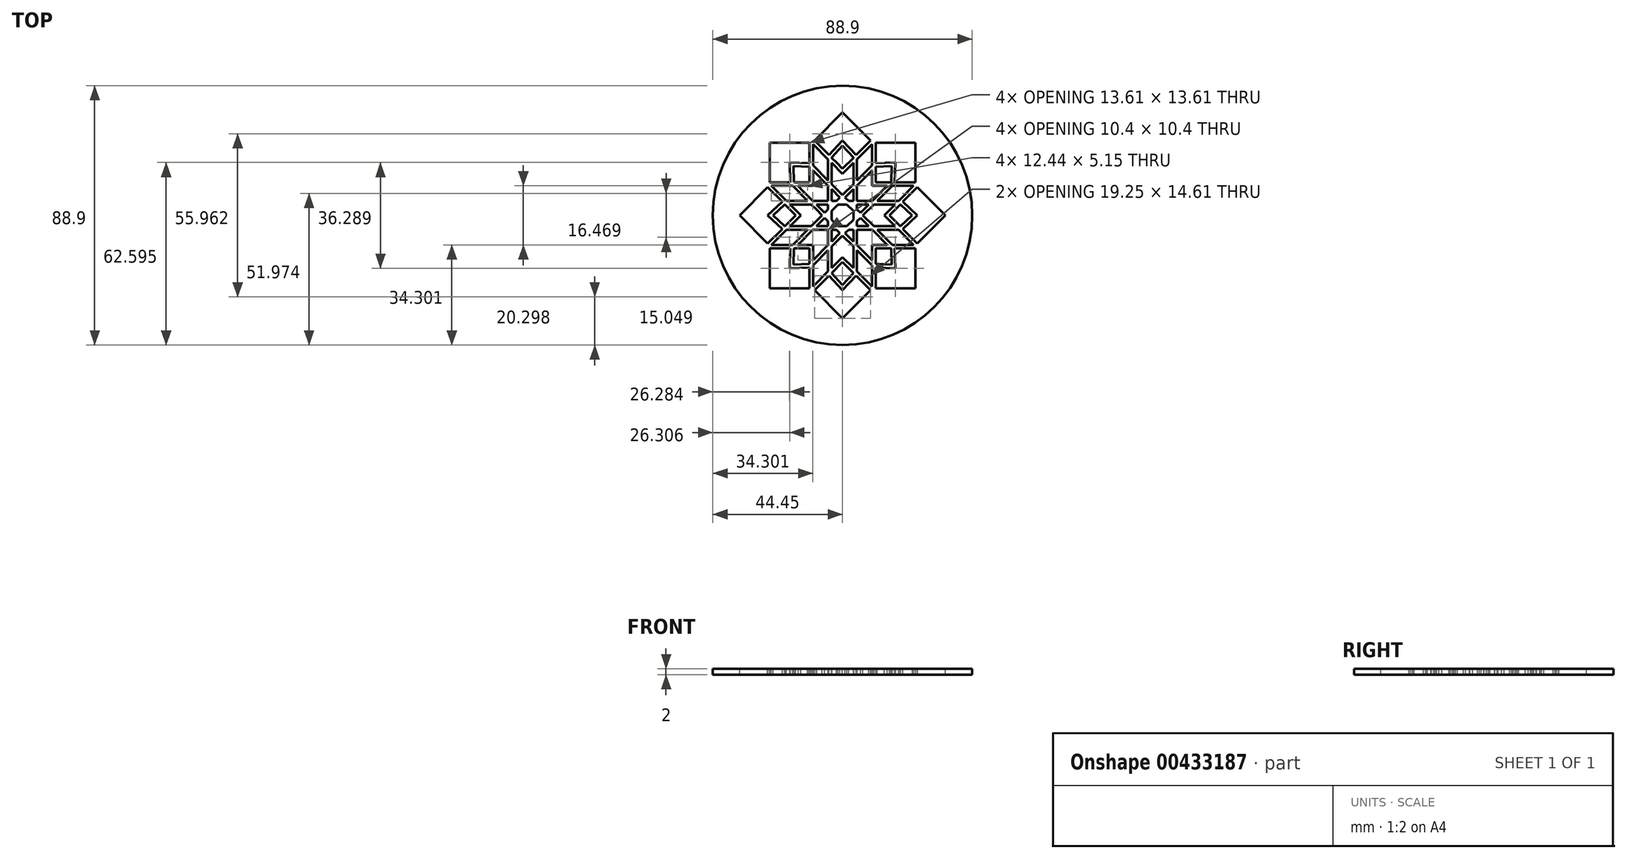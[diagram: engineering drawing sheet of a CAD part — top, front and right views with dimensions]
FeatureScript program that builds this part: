
annotation { "Feature Type Name" : "Feature", "Feature Type Description" : "" }
export const myFeature = defineFeature(function(context is Context, id is Id, definition is map)
    precondition{}
    {
        {
            var Q0;
            Q0=qCreatedBy(makeId("Top.planeOp"),FACE);
            var sketch = newSketch(context, id + "F0", { "sketchPlane" : qUnion([Q0])});
            skLineSegment(sketch, "E0.bottom", {"start": v(-44.45, 44.45) * mm, "end": v(44.45, 44.45) * mm});
            skLineSegment(sketch, "E0.top", {"start": v(-44.45, -44.45) * mm, "end": v(44.45, -44.45) * mm});
            skLineSegment(sketch, "E0.left", {"start": v(-44.45, 44.45) * mm, "end": v(-44.45, -44.45) * mm});
            skLineSegment(sketch, "E0.right", {"start": v(44.45, 44.45) * mm, "end": v(44.45, -44.45) * mm});
            skSolve(sketch);
        }
        {
            var Q0;
            Q0=qSketchRegion(id+"F0",true);
            extrude(context, id + "F1", {"entities" : qUnion([Q0]), "oppositeDirection" : true, "depth" : 2 * mm});
        }
        {
            var Q0;
            Q0=qCreatedBy(makeId("Top.planeOp"),FACE);
            var sketch = newSketch(context, id + "F2", { "sketchPlane" : qUnion([Q0])});
            skLineSegment(sketch, "E1", {"start": v(0.87, 6.12) * mm, "end": v(2.05, 4.95) * mm});
            skLineSegment(sketch, "E2", {"start": v(2.05, 4.95) * mm, "end": v(3.71, 4.95) * mm});
            skLineSegment(sketch, "E3", {"start": v(3.71, 4.95) * mm, "end": v(3.71, 8.96) * mm});
            skLineSegment(sketch, "E4", {"start": v(3.71, 8.96) * mm, "end": v(0.87, 6.12) * mm});
            skLineSegment(sketch, "E5", {"start": v(-3.71, 4.95) * mm, "end": v(-2.05, 4.95) * mm});
            skLineSegment(sketch, "E6", {"start": v(-2.05, 4.95) * mm, "end": v(-0.88, 6.12) * mm});
            skLineSegment(sketch, "E7", {"start": v(-0.88, 6.12) * mm, "end": v(-3.71, 8.96) * mm});
            skLineSegment(sketch, "E8", {"start": v(-3.71, 8.96) * mm, "end": v(-3.71, 4.95) * mm});
            skLineSegment(sketch, "E9", {"start": v(4.95, 3.71) * mm, "end": v(4.95, 2.05) * mm});
            skLineSegment(sketch, "E10", {"start": v(4.95, 2.05) * mm, "end": v(6.12, 0.88) * mm});
            skLineSegment(sketch, "E11", {"start": v(6.12, 0.88) * mm, "end": v(8.96, 3.71) * mm});
            skLineSegment(sketch, "E12", {"start": v(8.96, 3.71) * mm, "end": v(4.95, 3.71) * mm});
            skLineSegment(sketch, "E13", {"start": v(-0.88, -6.12) * mm, "end": v(-2.05, -4.95) * mm});
            skLineSegment(sketch, "E14", {"start": v(-2.05, -4.95) * mm, "end": v(-3.71, -4.95) * mm});
            skLineSegment(sketch, "E15", {"start": v(-3.71, -4.95) * mm, "end": v(-3.71, -8.96) * mm});
            skLineSegment(sketch, "E16", {"start": v(-3.71, -8.96) * mm, "end": v(-0.88, -6.12) * mm});
            skLineSegment(sketch, "E17", {"start": v(-4.95, -2.05) * mm, "end": v(-6.12, -0.87) * mm});
            skLineSegment(sketch, "E18", {"start": v(-6.12, -0.87) * mm, "end": v(-8.96, -3.71) * mm});
            skLineSegment(sketch, "E19", {"start": v(-8.96, -3.71) * mm, "end": v(-4.95, -3.71) * mm});
            skLineSegment(sketch, "E20", {"start": v(-4.95, -3.71) * mm, "end": v(-4.95, -2.05) * mm});
            skLineSegment(sketch, "E21", {"start": v(-14.28, 0) * mm, "end": v(-18, -3.71) * mm});
            skLineSegment(sketch, "E22", {"start": v(-18, -3.71) * mm, "end": v(-10.71, -3.71) * mm});
            skLineSegment(sketch, "E23", {"start": v(-10.71, -3.71) * mm, "end": v(-7, 0) * mm});
            skLineSegment(sketch, "E24", {"start": v(-7, 0) * mm, "end": v(-10.71, 3.71) * mm});
            skLineSegment(sketch, "E25", {"start": v(-10.71, 3.71) * mm, "end": v(-18, 3.71) * mm});
            skLineSegment(sketch, "E26", {"start": v(-18, 3.71) * mm, "end": v(-14.28, 0) * mm});
            skLineSegment(sketch, "E27", {"start": v(-8.96, 3.71) * mm, "end": v(-6.12, 0.88) * mm});
            skLineSegment(sketch, "E28", {"start": v(0, -7) * mm, "end": v(-3.71, -10.7) * mm});
            skLineSegment(sketch, "E29", {"start": v(-3.71, -10.7) * mm, "end": v(-3.71, -18) * mm});
            skLineSegment(sketch, "E30", {"start": v(-3.71, -18) * mm, "end": v(0, -14.28) * mm});
            skLineSegment(sketch, "E31", {"start": v(0, -14.28) * mm, "end": v(3.71, -18) * mm});
            skLineSegment(sketch, "E32", {"start": v(3.71, -18) * mm, "end": v(3.71, -10.7) * mm});
            skLineSegment(sketch, "E33", {"start": v(3.71, -10.7) * mm, "end": v(0, -7) * mm});
            skLineSegment(sketch, "E34", {"start": v(-10.1, -17.1) * mm, "end": v(-10.1, -24.38) * mm});
            skLineSegment(sketch, "E35", {"start": v(-10.1, -24.38) * mm, "end": v(-4.95, -19.23) * mm});
            skLineSegment(sketch, "E36", {"start": v(-4.95, -19.23) * mm, "end": v(-4.95, -11.95) * mm});
            skLineSegment(sketch, "E37", {"start": v(-4.95, -11.95) * mm, "end": v(-10.1, -17.1) * mm});
            skLineSegment(sketch, "E38", {"start": v(1.54, -3.71) * mm, "end": v(3.71, -1.54) * mm});
            skLineSegment(sketch, "E39", {"start": v(3.71, -1.54) * mm, "end": v(3.71, 1.54) * mm});
            skLineSegment(sketch, "E40", {"start": v(3.71, 1.54) * mm, "end": v(1.54, 3.71) * mm});
            skLineSegment(sketch, "E41", {"start": v(1.54, 3.71) * mm, "end": v(-1.54, 3.71) * mm});
            skLineSegment(sketch, "E42", {"start": v(-1.54, 3.71) * mm, "end": v(-3.71, 1.54) * mm});
            skLineSegment(sketch, "E43", {"start": v(-3.71, 1.54) * mm, "end": v(-3.71, -1.54) * mm});
            skLineSegment(sketch, "E44", {"start": v(-3.71, -1.54) * mm, "end": v(-1.54, -3.71) * mm});
            skLineSegment(sketch, "E45", {"start": v(-1.54, -3.71) * mm, "end": v(1.54, -3.71) * mm});
            skLineSegment(sketch, "E46", {"start": v(3.71, -19.86) * mm, "end": v(3.71, -19.75) * mm});
            skLineSegment(sketch, "E47", {"start": v(3.71, -19.75) * mm, "end": v(0, -16.03) * mm});
            skLineSegment(sketch, "E48", {"start": v(0, -16.03) * mm, "end": v(-3.71, -19.74) * mm});
            skLineSegment(sketch, "E49", {"start": v(-3.71, -19.74) * mm, "end": v(-3.71, -19.86) * mm});
            skLineSegment(sketch, "E50", {"start": v(-3.71, -19.86) * mm, "end": v(0, -23.84) * mm});
            skLineSegment(sketch, "E51", {"start": v(0, -23.84) * mm, "end": v(3.71, -19.86) * mm});
            skLineSegment(sketch, "E52", {"start": v(11.34, -16.59) * mm, "end": v(11.42, -16.67) * mm});
            skLineSegment(sketch, "E53", {"start": v(11.42, -16.67) * mm, "end": v(16.86, -16.86) * mm});
            skLineSegment(sketch, "E54", {"start": v(16.86, -16.86) * mm, "end": v(16.67, -11.42) * mm});
            skLineSegment(sketch, "E55", {"start": v(16.67, -11.42) * mm, "end": v(16.59, -11.34) * mm});
            skLineSegment(sketch, "E56", {"start": v(16.59, -11.34) * mm, "end": v(11.34, -11.34) * mm});
            skLineSegment(sketch, "E57", {"start": v(11.34, -11.34) * mm, "end": v(11.34, -16.59) * mm});
            skLineSegment(sketch, "E58", {"start": v(-19.75, 3.71) * mm, "end": v(-19.86, 3.71) * mm});
            skLineSegment(sketch, "E59", {"start": v(-19.86, 3.71) * mm, "end": v(-23.84, 0) * mm});
            skLineSegment(sketch, "E60", {"start": v(-23.84, 0) * mm, "end": v(-19.86, -3.71) * mm});
            skLineSegment(sketch, "E61", {"start": v(-19.86, -3.71) * mm, "end": v(-19.75, -3.71) * mm});
            skLineSegment(sketch, "E62", {"start": v(-19.75, -3.71) * mm, "end": v(-16.03, 0) * mm});
            skLineSegment(sketch, "E63", {"start": v(-16.03, 0) * mm, "end": v(-19.75, 3.71) * mm});
            skLineSegment(sketch, "E64", {"start": v(10.1, 17.1) * mm, "end": v(10.1, 24.39) * mm});
            skLineSegment(sketch, "E65", {"start": v(10.1, 24.39) * mm, "end": v(4.95, 19.23) * mm});
            skLineSegment(sketch, "E66", {"start": v(4.95, 19.23) * mm, "end": v(4.95, 11.95) * mm});
            skLineSegment(sketch, "E67", {"start": v(4.95, 11.95) * mm, "end": v(10.1, 17.1) * mm});
            skLineSegment(sketch, "E68", {"start": v(19.75, -3.71) * mm, "end": v(19.86, -3.71) * mm});
            skLineSegment(sketch, "E69", {"start": v(19.86, -3.71) * mm, "end": v(23.84, 0) * mm});
            skLineSegment(sketch, "E70", {"start": v(23.84, 0) * mm, "end": v(19.86, 3.71) * mm});
            skLineSegment(sketch, "E71", {"start": v(19.86, 3.71) * mm, "end": v(19.75, 3.71) * mm});
            skLineSegment(sketch, "E72", {"start": v(19.75, 3.71) * mm, "end": v(16.03, 0) * mm});
            skLineSegment(sketch, "E73", {"start": v(16.03, 0) * mm, "end": v(19.75, -3.71) * mm});
            skLineSegment(sketch, "E74", {"start": v(0, 7) * mm, "end": v(3.71, 10.71) * mm});
            skLineSegment(sketch, "E75", {"start": v(3.71, 10.71) * mm, "end": v(3.71, 18) * mm});
            skLineSegment(sketch, "E76", {"start": v(3.71, 18) * mm, "end": v(0, 14.29) * mm});
            skLineSegment(sketch, "E77", {"start": v(0, 14.29) * mm, "end": v(-3.71, 18) * mm});
            skLineSegment(sketch, "E78", {"start": v(-3.71, 18) * mm, "end": v(-3.71, 10.71) * mm});
            skLineSegment(sketch, "E79", {"start": v(-3.71, 10.71) * mm, "end": v(0, 7) * mm});
            skLineSegment(sketch, "E80", {"start": v(-3.71, 19.86) * mm, "end": v(-3.71, 19.75) * mm});
            skLineSegment(sketch, "E81", {"start": v(-3.71, 19.75) * mm, "end": v(0, 16.03) * mm});
            skLineSegment(sketch, "E82", {"start": v(0, 16.03) * mm, "end": v(3.71, 19.75) * mm});
            skLineSegment(sketch, "E83", {"start": v(3.71, 19.75) * mm, "end": v(3.71, 19.86) * mm});
            skLineSegment(sketch, "E84", {"start": v(3.71, 19.86) * mm, "end": v(0, 23.84) * mm});
            skLineSegment(sketch, "E85", {"start": v(0, 23.84) * mm, "end": v(-3.71, 19.86) * mm});
            skLineSegment(sketch, "E86", {"start": v(10.1, -17.1) * mm, "end": v(4.95, -11.95) * mm});
            skLineSegment(sketch, "E87", {"start": v(4.95, -11.95) * mm, "end": v(4.95, -19.23) * mm});
            skLineSegment(sketch, "E88", {"start": v(4.95, -19.23) * mm, "end": v(10.1, -24.38) * mm});
            skLineSegment(sketch, "E89", {"start": v(10.1, -24.38) * mm, "end": v(10.1, -17.1) * mm});
            skLineSegment(sketch, "E90", {"start": v(11.34, 17.9) * mm, "end": v(18.14, 18.14) * mm});
            skLineSegment(sketch, "E91", {"start": v(18.14, 18.14) * mm, "end": v(17.9, 11.34) * mm});
            skLineSegment(sketch, "E92", {"start": v(17.9, 11.34) * mm, "end": v(24.95, 11.34) * mm});
            skLineSegment(sketch, "E93", {"start": v(24.95, 11.34) * mm, "end": v(24.95, 24.95) * mm});
            skLineSegment(sketch, "E94", {"start": v(24.95, 24.95) * mm, "end": v(11.34, 24.95) * mm});
            skLineSegment(sketch, "E95", {"start": v(11.34, 24.95) * mm, "end": v(11.34, 17.9) * mm});
            skLineSegment(sketch, "E96", {"start": v(0, 25.65) * mm, "end": v(4.64, 20.68) * mm});
            skLineSegment(sketch, "E97", {"start": v(4.64, 20.68) * mm, "end": v(9.63, 25.66) * mm});
            skLineSegment(sketch, "E98", {"start": v(9.63, 25.66) * mm, "end": v(0, 35.29) * mm});
            skLineSegment(sketch, "E99", {"start": v(0, 35.29) * mm, "end": v(-9.63, 25.66) * mm});
            skLineSegment(sketch, "E100", {"start": v(-9.63, 25.66) * mm, "end": v(-4.64, 20.68) * mm});
            skLineSegment(sketch, "E101", {"start": v(-4.64, 20.68) * mm, "end": v(0, 25.65) * mm});
            skLineSegment(sketch, "E102", {"start": v(20.68, 4.64) * mm, "end": v(25.65, 0) * mm});
            skLineSegment(sketch, "E103", {"start": v(25.65, 0) * mm, "end": v(20.68, -4.64) * mm});
            skLineSegment(sketch, "E104", {"start": v(20.68, -4.64) * mm, "end": v(25.66, -9.63) * mm});
            skLineSegment(sketch, "E105", {"start": v(25.66, -9.63) * mm, "end": v(35.29, 0) * mm});
            skLineSegment(sketch, "E106", {"start": v(35.29, 0) * mm, "end": v(25.66, 9.63) * mm});
            skLineSegment(sketch, "E107", {"start": v(25.66, 9.63) * mm, "end": v(20.68, 4.64) * mm});
            skLineSegment(sketch, "E108", {"start": v(-18.14, 18.14) * mm, "end": v(-11.34, 17.9) * mm});
            skLineSegment(sketch, "E109", {"start": v(-11.34, 17.9) * mm, "end": v(-11.34, 24.95) * mm});
            skLineSegment(sketch, "E110", {"start": v(-11.34, 24.95) * mm, "end": v(-24.95, 24.95) * mm});
            skLineSegment(sketch, "E111", {"start": v(-24.95, 24.95) * mm, "end": v(-24.95, 11.34) * mm});
            skLineSegment(sketch, "E112", {"start": v(-24.95, 11.34) * mm, "end": v(-17.9, 11.34) * mm});
            skLineSegment(sketch, "E113", {"start": v(-17.9, 11.34) * mm, "end": v(-18.14, 18.14) * mm});
            skLineSegment(sketch, "E114", {"start": v(15.35, -10.1) * mm, "end": v(10.2, -4.95) * mm});
            skLineSegment(sketch, "E115", {"start": v(10.2, -4.95) * mm, "end": v(4.95, -4.95) * mm});
            skLineSegment(sketch, "E116", {"start": v(4.95, -4.95) * mm, "end": v(4.95, -10.2) * mm});
            skLineSegment(sketch, "E117", {"start": v(4.95, -10.2) * mm, "end": v(10.1, -15.35) * mm});
            skLineSegment(sketch, "E118", {"start": v(10.1, -15.35) * mm, "end": v(10.1, -10.1) * mm});
            skLineSegment(sketch, "E119", {"start": v(10.1, -10.1) * mm, "end": v(15.35, -10.1) * mm});
            skLineSegment(sketch, "E120", {"start": v(19.23, -4.95) * mm, "end": v(11.95, -4.95) * mm});
            skLineSegment(sketch, "E121", {"start": v(11.95, -4.95) * mm, "end": v(17.1, -10.1) * mm});
            skLineSegment(sketch, "E122", {"start": v(17.1, -10.1) * mm, "end": v(24.38, -10.1) * mm});
            skLineSegment(sketch, "E123", {"start": v(24.38, -10.1) * mm, "end": v(19.23, -4.95) * mm});
            skLineSegment(sketch, "E124", {"start": v(-20.68, -4.64) * mm, "end": v(-25.65, 0) * mm});
            skLineSegment(sketch, "E125", {"start": v(-25.65, 0) * mm, "end": v(-20.68, 4.64) * mm});
            skLineSegment(sketch, "E126", {"start": v(-20.68, 4.64) * mm, "end": v(-25.66, 9.63) * mm});
            skLineSegment(sketch, "E127", {"start": v(-25.66, 9.63) * mm, "end": v(-35.29, 0) * mm});
            skLineSegment(sketch, "E128", {"start": v(-35.29, 0) * mm, "end": v(-25.66, -9.63) * mm});
            skLineSegment(sketch, "E129", {"start": v(-25.66, -9.63) * mm, "end": v(-20.68, -4.64) * mm});
            skLineSegment(sketch, "E130", {"start": v(-4.95, -10.2) * mm, "end": v(-4.95, -4.95) * mm});
            skLineSegment(sketch, "E131", {"start": v(-4.95, -4.95) * mm, "end": v(-10.2, -4.95) * mm});
            skLineSegment(sketch, "E132", {"start": v(-10.2, -4.95) * mm, "end": v(-15.35, -10.1) * mm});
            skLineSegment(sketch, "E133", {"start": v(-15.35, -10.1) * mm, "end": v(-10.1, -10.1) * mm});
            skLineSegment(sketch, "E134", {"start": v(-10.1, -10.1) * mm, "end": v(-10.1, -15.35) * mm});
            skLineSegment(sketch, "E135", {"start": v(-10.1, -15.35) * mm, "end": v(-4.95, -10.2) * mm});
            skLineSegment(sketch, "E136", {"start": v(3.71, -4.95) * mm, "end": v(2.05, -4.95) * mm});
            skLineSegment(sketch, "E137", {"start": v(2.05, -4.95) * mm, "end": v(0.87, -6.12) * mm});
            skLineSegment(sketch, "E138", {"start": v(0.87, -6.12) * mm, "end": v(3.71, -8.96) * mm});
            skLineSegment(sketch, "E139", {"start": v(3.71, -8.96) * mm, "end": v(3.71, -4.95) * mm});
            skLineSegment(sketch, "E140", {"start": v(0, -35.29) * mm, "end": v(9.63, -25.66) * mm});
            skLineSegment(sketch, "E141", {"start": v(9.63, -25.66) * mm, "end": v(4.64, -20.68) * mm});
            skLineSegment(sketch, "E142", {"start": v(4.64, -20.68) * mm, "end": v(0, -25.65) * mm});
            skLineSegment(sketch, "E143", {"start": v(0, -25.65) * mm, "end": v(-4.64, -20.68) * mm});
            skLineSegment(sketch, "E144", {"start": v(-4.64, -20.68) * mm, "end": v(-9.63, -25.66) * mm});
            skLineSegment(sketch, "E145", {"start": v(-9.63, -25.66) * mm, "end": v(0, -35.29) * mm});
            skLineSegment(sketch, "E146", {"start": v(18.14, -18.14) * mm, "end": v(11.34, -17.9) * mm});
            skLineSegment(sketch, "E147", {"start": v(11.34, -17.9) * mm, "end": v(11.34, -24.95) * mm});
            skLineSegment(sketch, "E148", {"start": v(11.34, -24.95) * mm, "end": v(24.95, -24.95) * mm});
            skLineSegment(sketch, "E149", {"start": v(24.95, -24.95) * mm, "end": v(24.95, -11.34) * mm});
            skLineSegment(sketch, "E150", {"start": v(24.95, -11.34) * mm, "end": v(17.9, -11.34) * mm});
            skLineSegment(sketch, "E151", {"start": v(17.9, -11.34) * mm, "end": v(18.14, -18.14) * mm});
            skLineSegment(sketch, "E152", {"start": v(14.28, 0) * mm, "end": v(18, 3.71) * mm});
            skLineSegment(sketch, "E153", {"start": v(18, 3.71) * mm, "end": v(10.7, 3.71) * mm});
            skLineSegment(sketch, "E154", {"start": v(10.7, 3.71) * mm, "end": v(7, 0) * mm});
            skLineSegment(sketch, "E155", {"start": v(7, 0) * mm, "end": v(10.7, -3.71) * mm});
            skLineSegment(sketch, "E156", {"start": v(10.7, -3.71) * mm, "end": v(18, -3.71) * mm});
            skLineSegment(sketch, "E157", {"start": v(18, -3.71) * mm, "end": v(14.28, 0) * mm});
            skLineSegment(sketch, "E158", {"start": v(4.95, 10.2) * mm, "end": v(4.95, 4.95) * mm});
            skLineSegment(sketch, "E159", {"start": v(4.95, 4.95) * mm, "end": v(10.2, 4.95) * mm});
            skLineSegment(sketch, "E160", {"start": v(10.2, 4.95) * mm, "end": v(15.35, 10.1) * mm});
            skLineSegment(sketch, "E161", {"start": v(15.35, 10.1) * mm, "end": v(10.1, 10.1) * mm});
            skLineSegment(sketch, "E162", {"start": v(10.1, 10.1) * mm, "end": v(10.1, 15.35) * mm});
            skLineSegment(sketch, "E163", {"start": v(10.1, 15.35) * mm, "end": v(4.95, 10.2) * mm});
            skLineSegment(sketch, "E164", {"start": v(11.34, 16.59) * mm, "end": v(11.34, 11.34) * mm});
            skLineSegment(sketch, "E165", {"start": v(11.34, 11.34) * mm, "end": v(16.59, 11.34) * mm});
            skLineSegment(sketch, "E166", {"start": v(16.59, 11.34) * mm, "end": v(16.67, 11.42) * mm});
            skLineSegment(sketch, "E167", {"start": v(16.67, 11.42) * mm, "end": v(16.86, 16.86) * mm});
            skLineSegment(sketch, "E168", {"start": v(16.86, 16.86) * mm, "end": v(11.42, 16.67) * mm});
            skLineSegment(sketch, "E169", {"start": v(11.42, 16.67) * mm, "end": v(11.34, 16.59) * mm});
            skLineSegment(sketch, "E170", {"start": v(17.1, 10.1) * mm, "end": v(11.95, 4.95) * mm});
            skLineSegment(sketch, "E171", {"start": v(11.95, 4.95) * mm, "end": v(19.23, 4.95) * mm});
            skLineSegment(sketch, "E172", {"start": v(19.23, 4.95) * mm, "end": v(24.38, 10.1) * mm});
            skLineSegment(sketch, "E173", {"start": v(24.38, 10.1) * mm, "end": v(17.1, 10.1) * mm});
            skLineSegment(sketch, "E174", {"start": v(6.12, -0.87) * mm, "end": v(4.95, -2.05) * mm});
            skLineSegment(sketch, "E175", {"start": v(4.95, -2.05) * mm, "end": v(4.95, -3.71) * mm});
            skLineSegment(sketch, "E176", {"start": v(4.95, -3.71) * mm, "end": v(8.96, -3.71) * mm});
            skLineSegment(sketch, "E177", {"start": v(8.96, -3.71) * mm, "end": v(6.12, -0.87) * mm});
            skLineSegment(sketch, "E178", {"start": v(-24.38, -10.1) * mm, "end": v(-17.1, -10.1) * mm});
            skLineSegment(sketch, "E179", {"start": v(-10.1, 17.1) * mm, "end": v(-4.95, 11.95) * mm});
            skLineSegment(sketch, "E180", {"start": v(-4.95, 11.95) * mm, "end": v(-4.95, 19.23) * mm});
            skLineSegment(sketch, "E181", {"start": v(-4.95, 19.23) * mm, "end": v(-10.1, 24.39) * mm});
            skLineSegment(sketch, "E182", {"start": v(-10.1, 24.39) * mm, "end": v(-10.1, 17.1) * mm});
            skLineSegment(sketch, "E183", {"start": v(-19.23, 4.95) * mm, "end": v(-11.95, 4.95) * mm});
            skLineSegment(sketch, "E184", {"start": v(-11.95, 4.95) * mm, "end": v(-17.1, 10.1) * mm});
            skLineSegment(sketch, "E185", {"start": v(-17.1, 10.1) * mm, "end": v(-24.39, 10.1) * mm});
            skLineSegment(sketch, "E186", {"start": v(-24.39, 10.1) * mm, "end": v(-19.23, 4.95) * mm});
            skLineSegment(sketch, "E187", {"start": v(-15.35, 10.1) * mm, "end": v(-10.2, 4.95) * mm});
            skLineSegment(sketch, "E188", {"start": v(-10.2, 4.95) * mm, "end": v(-4.95, 4.95) * mm});
            skLineSegment(sketch, "E189", {"start": v(-4.95, 4.95) * mm, "end": v(-4.95, 10.2) * mm});
            skLineSegment(sketch, "E190", {"start": v(-4.95, 10.2) * mm, "end": v(-10.1, 15.35) * mm});
            skLineSegment(sketch, "E191", {"start": v(-10.1, 15.35) * mm, "end": v(-10.1, 10.1) * mm});
            skLineSegment(sketch, "E192", {"start": v(-10.1, 10.1) * mm, "end": v(-15.35, 10.1) * mm});
            skLineSegment(sketch, "E193", {"start": v(-11.34, -16.59) * mm, "end": v(-11.34, -11.34) * mm});
            skLineSegment(sketch, "E194", {"start": v(-11.34, -11.34) * mm, "end": v(-16.59, -11.34) * mm});
            skLineSegment(sketch, "E195", {"start": v(-16.59, -11.34) * mm, "end": v(-16.67, -11.42) * mm});
            skLineSegment(sketch, "E196", {"start": v(-16.67, -11.42) * mm, "end": v(-16.86, -16.86) * mm});
            skLineSegment(sketch, "E197", {"start": v(-16.86, -16.86) * mm, "end": v(-11.42, -16.67) * mm});
            skLineSegment(sketch, "E198", {"start": v(-11.42, -16.67) * mm, "end": v(-11.34, -16.59) * mm});
            skLineSegment(sketch, "E199", {"start": v(16.67, -11.42) * mm, "end": v(16.86, -16.86) * mm});
            skLineSegment(sketch, "E200", {"start": v(16.86, -16.86) * mm, "end": v(11.42, -16.67) * mm});
            skLineSegment(sketch, "E201", {"start": v(11.42, -16.67) * mm, "end": v(11.34, -16.59) * mm});
            skLineSegment(sketch, "E202", {"start": v(11.34, -16.59) * mm, "end": v(11.34, -11.34) * mm});
            skLineSegment(sketch, "E203", {"start": v(11.34, -11.34) * mm, "end": v(16.59, -11.34) * mm});
            skLineSegment(sketch, "E204", {"start": v(16.59, -11.34) * mm, "end": v(16.67, -11.42) * mm});
            skLineSegment(sketch, "E205", {"start": v(-3.71, -19.74) * mm, "end": v(0, -16.03) * mm});
            skLineSegment(sketch, "E206", {"start": v(0, -16.03) * mm, "end": v(3.71, -19.75) * mm});
            skLineSegment(sketch, "E207", {"start": v(3.71, -19.75) * mm, "end": v(3.71, -19.86) * mm});
            skLineSegment(sketch, "E208", {"start": v(3.71, -19.86) * mm, "end": v(0, -23.84) * mm});
            skLineSegment(sketch, "E209", {"start": v(0, -23.84) * mm, "end": v(-3.71, -19.86) * mm});
            skLineSegment(sketch, "E210", {"start": v(-3.71, -19.86) * mm, "end": v(-3.71, -19.74) * mm});
            skLineSegment(sketch, "E211", {"start": v(0, -14.28) * mm, "end": v(-3.71, -18) * mm});
            skLineSegment(sketch, "E212", {"start": v(-3.71, -18) * mm, "end": v(-3.71, -10.7) * mm});
            skLineSegment(sketch, "E213", {"start": v(-3.71, -10.7) * mm, "end": v(0, -7) * mm});
            skLineSegment(sketch, "E214", {"start": v(0, -7) * mm, "end": v(3.71, -10.7) * mm});
            skLineSegment(sketch, "E215", {"start": v(3.71, -10.7) * mm, "end": v(3.71, -18) * mm});
            skLineSegment(sketch, "E216", {"start": v(3.71, -18) * mm, "end": v(0, -14.28) * mm});
            skLineSegment(sketch, "E217", {"start": v(-10.1, -24.38) * mm, "end": v(-10.1, -17.1) * mm});
            skLineSegment(sketch, "E218", {"start": v(-10.1, -17.1) * mm, "end": v(-4.95, -11.95) * mm});
            skLineSegment(sketch, "E219", {"start": v(-4.95, -11.95) * mm, "end": v(-4.95, -19.23) * mm});
            skLineSegment(sketch, "E220", {"start": v(-4.95, -19.23) * mm, "end": v(-10.1, -24.38) * mm});
            skLineSegment(sketch, "E221", {"start": v(-19.86, -3.71) * mm, "end": v(-23.84, 0) * mm});
            skLineSegment(sketch, "E222", {"start": v(-23.84, 0) * mm, "end": v(-19.86, 3.71) * mm});
            skLineSegment(sketch, "E223", {"start": v(-19.86, 3.71) * mm, "end": v(-19.75, 3.71) * mm});
            skLineSegment(sketch, "E224", {"start": v(-19.75, 3.71) * mm, "end": v(-16.03, 0) * mm});
            skLineSegment(sketch, "E225", {"start": v(-16.03, 0) * mm, "end": v(-19.75, -3.71) * mm});
            skLineSegment(sketch, "E226", {"start": v(-19.75, -3.71) * mm, "end": v(-19.86, -3.71) * mm});
            skLineSegment(sketch, "E227", {"start": v(3.71, 19.75) * mm, "end": v(0, 16.03) * mm});
            skLineSegment(sketch, "E228", {"start": v(0, 16.03) * mm, "end": v(-3.71, 19.75) * mm});
            skLineSegment(sketch, "E229", {"start": v(-3.71, 19.75) * mm, "end": v(-3.71, 19.86) * mm});
            skLineSegment(sketch, "E230", {"start": v(-3.71, 19.86) * mm, "end": v(0, 23.84) * mm});
            skLineSegment(sketch, "E231", {"start": v(0, 23.84) * mm, "end": v(3.71, 19.86) * mm});
            skLineSegment(sketch, "E232", {"start": v(3.71, 19.86) * mm, "end": v(3.71, 19.75) * mm});
            skLineSegment(sketch, "E233", {"start": v(0, 14.28) * mm, "end": v(3.71, 18) * mm});
            skLineSegment(sketch, "E234", {"start": v(3.71, 18) * mm, "end": v(3.71, 10.71) * mm});
            skLineSegment(sketch, "E235", {"start": v(3.71, 10.71) * mm, "end": v(0, 7) * mm});
            skLineSegment(sketch, "E236", {"start": v(0, 7) * mm, "end": v(-3.71, 10.71) * mm});
            skLineSegment(sketch, "E237", {"start": v(-3.71, 10.71) * mm, "end": v(-3.71, 18) * mm});
            skLineSegment(sketch, "E238", {"start": v(-3.71, 18) * mm, "end": v(0, 14.28) * mm});
            skLineSegment(sketch, "E239", {"start": v(10.1, 24.39) * mm, "end": v(10.1, 17.1) * mm});
            skLineSegment(sketch, "E240", {"start": v(10.1, 17.1) * mm, "end": v(4.95, 11.95) * mm});
            skLineSegment(sketch, "E241", {"start": v(4.95, 11.95) * mm, "end": v(4.95, 19.23) * mm});
            skLineSegment(sketch, "E242", {"start": v(4.95, 19.23) * mm, "end": v(10.1, 24.39) * mm});
            skLineSegment(sketch, "E243", {"start": v(19.86, 3.71) * mm, "end": v(23.84, 0) * mm});
            skLineSegment(sketch, "E244", {"start": v(23.84, 0) * mm, "end": v(19.86, -3.71) * mm});
            skLineSegment(sketch, "E245", {"start": v(19.86, -3.71) * mm, "end": v(19.75, -3.71) * mm});
            skLineSegment(sketch, "E246", {"start": v(19.75, -3.71) * mm, "end": v(16.03, 0) * mm});
            skLineSegment(sketch, "E247", {"start": v(16.03, 0) * mm, "end": v(19.75, 3.71) * mm});
            skLineSegment(sketch, "E248", {"start": v(19.75, 3.71) * mm, "end": v(19.86, 3.71) * mm});
            skLineSegment(sketch, "E249", {"start": v(-3.71, 1.54) * mm, "end": v(-1.54, 3.71) * mm});
            skLineSegment(sketch, "E250", {"start": v(-1.54, 3.71) * mm, "end": v(1.54, 3.71) * mm});
            skLineSegment(sketch, "E251", {"start": v(1.54, 3.71) * mm, "end": v(3.71, 1.54) * mm});
            skLineSegment(sketch, "E252", {"start": v(3.71, 1.54) * mm, "end": v(3.71, -1.54) * mm});
            skLineSegment(sketch, "E253", {"start": v(3.71, -1.54) * mm, "end": v(1.54, -3.71) * mm});
            skLineSegment(sketch, "E254", {"start": v(1.54, -3.71) * mm, "end": v(-1.54, -3.71) * mm});
            skLineSegment(sketch, "E255", {"start": v(-1.54, -3.71) * mm, "end": v(-3.71, -1.54) * mm});
            skLineSegment(sketch, "E256", {"start": v(-3.71, -1.54) * mm, "end": v(-3.71, 1.54) * mm});
            skLineSegment(sketch, "E257", {"start": v(4.95, 2.05) * mm, "end": v(4.95, 3.71) * mm});
            skLineSegment(sketch, "E258", {"start": v(4.95, 3.71) * mm, "end": v(8.96, 3.71) * mm});
            skLineSegment(sketch, "E259", {"start": v(8.96, 3.71) * mm, "end": v(6.12, 0.88) * mm});
            skLineSegment(sketch, "E260", {"start": v(6.12, 0.88) * mm, "end": v(4.95, 2.05) * mm});
            skLineSegment(sketch, "E261", {"start": v(2.05, 4.95) * mm, "end": v(0.87, 6.12) * mm});
            skLineSegment(sketch, "E262", {"start": v(0.87, 6.12) * mm, "end": v(3.71, 8.96) * mm});
            skLineSegment(sketch, "E263", {"start": v(3.71, 8.96) * mm, "end": v(3.71, 4.95) * mm});
            skLineSegment(sketch, "E264", {"start": v(3.71, 4.95) * mm, "end": v(2.05, 4.95) * mm});
            skLineSegment(sketch, "E265", {"start": v(-2.05, 4.95) * mm, "end": v(-3.71, 4.95) * mm});
            skLineSegment(sketch, "E266", {"start": v(-3.71, 4.95) * mm, "end": v(-3.71, 8.96) * mm});
            skLineSegment(sketch, "E267", {"start": v(-3.71, 8.96) * mm, "end": v(-0.88, 6.12) * mm});
            skLineSegment(sketch, "E268", {"start": v(-0.88, 6.12) * mm, "end": v(-2.05, 4.95) * mm});
            skLineSegment(sketch, "E269", {"start": v(-4.95, 2.05) * mm, "end": v(-6.12, 0.88) * mm});
            skLineSegment(sketch, "E270", {"start": v(-8.96, 3.71) * mm, "end": v(-4.95, 3.71) * mm});
            skLineSegment(sketch, "E271", {"start": v(-4.95, 3.71) * mm, "end": v(-4.95, 2.05) * mm});
            skLineSegment(sketch, "E272", {"start": v(-7, 0) * mm, "end": v(-10.71, -3.71) * mm});
            skLineSegment(sketch, "E273", {"start": v(-10.71, -3.71) * mm, "end": v(-18, -3.71) * mm});
            skLineSegment(sketch, "E274", {"start": v(-18, -3.71) * mm, "end": v(-14.29, 0) * mm});
            skLineSegment(sketch, "E275", {"start": v(-14.29, 0) * mm, "end": v(-18, 3.71) * mm});
            skLineSegment(sketch, "E276", {"start": v(-18, 3.71) * mm, "end": v(-10.71, 3.71) * mm});
            skLineSegment(sketch, "E277", {"start": v(-10.71, 3.71) * mm, "end": v(-7, 0) * mm});
            skLineSegment(sketch, "E278", {"start": v(-6.12, -0.87) * mm, "end": v(-4.95, -2.05) * mm});
            skLineSegment(sketch, "E279", {"start": v(-4.95, -2.05) * mm, "end": v(-4.95, -3.71) * mm});
            skLineSegment(sketch, "E280", {"start": v(-4.95, -3.71) * mm, "end": v(-8.96, -3.71) * mm});
            skLineSegment(sketch, "E281", {"start": v(-8.96, -3.71) * mm, "end": v(-6.12, -0.87) * mm});
            skLineSegment(sketch, "E282", {"start": v(-2.05, -4.95) * mm, "end": v(-0.88, -6.12) * mm});
            skLineSegment(sketch, "E283", {"start": v(-0.88, -6.12) * mm, "end": v(-3.71, -8.96) * mm});
            skLineSegment(sketch, "E284", {"start": v(-3.71, -8.96) * mm, "end": v(-3.71, -4.95) * mm});
            skLineSegment(sketch, "E285", {"start": v(-3.71, -4.95) * mm, "end": v(-2.05, -4.95) * mm});
            skLineSegment(sketch, "E286", {"start": v(2.05, -4.95) * mm, "end": v(3.71, -4.95) * mm});
            skLineSegment(sketch, "E287", {"start": v(3.71, -4.95) * mm, "end": v(3.71, -8.96) * mm});
            skLineSegment(sketch, "E288", {"start": v(3.71, -8.96) * mm, "end": v(0.87, -6.12) * mm});
            skLineSegment(sketch, "E289", {"start": v(0.87, -6.12) * mm, "end": v(2.05, -4.95) * mm});
            skLineSegment(sketch, "E290", {"start": v(4.95, -2.05) * mm, "end": v(6.12, -0.87) * mm});
            skLineSegment(sketch, "E291", {"start": v(6.12, -0.87) * mm, "end": v(8.96, -3.71) * mm});
            skLineSegment(sketch, "E292", {"start": v(8.96, -3.71) * mm, "end": v(4.95, -3.71) * mm});
            skLineSegment(sketch, "E293", {"start": v(18, 3.71) * mm, "end": v(14.28, 0) * mm});
            skLineSegment(sketch, "E294", {"start": v(14.28, 0) * mm, "end": v(18, -3.71) * mm});
            skLineSegment(sketch, "E295", {"start": v(18, -3.71) * mm, "end": v(10.7, -3.71) * mm});
            skLineSegment(sketch, "E296", {"start": v(10.7, -3.71) * mm, "end": v(7, 0) * mm});
            skLineSegment(sketch, "E297", {"start": v(19.23, 4.95) * mm, "end": v(11.95, 4.95) * mm});
            skLineSegment(sketch, "E298", {"start": v(11.95, 4.95) * mm, "end": v(17.1, 10.1) * mm});
            skLineSegment(sketch, "E299", {"start": v(17.1, 10.1) * mm, "end": v(24.38, 10.1) * mm});
            skLineSegment(sketch, "E300", {"start": v(24.38, 10.1) * mm, "end": v(19.23, 4.95) * mm});
            skLineSegment(sketch, "E301", {"start": v(16.67, 11.42) * mm, "end": v(16.59, 11.34) * mm});
            skLineSegment(sketch, "E302", {"start": v(16.59, 11.34) * mm, "end": v(11.34, 11.34) * mm});
            skLineSegment(sketch, "E303", {"start": v(11.34, 11.34) * mm, "end": v(11.34, 16.59) * mm});
            skLineSegment(sketch, "E304", {"start": v(11.34, 16.59) * mm, "end": v(11.42, 16.67) * mm});
            skLineSegment(sketch, "E305", {"start": v(11.42, 16.67) * mm, "end": v(16.86, 16.86) * mm});
            skLineSegment(sketch, "E306", {"start": v(16.86, 16.86) * mm, "end": v(16.67, 11.42) * mm});
            skLineSegment(sketch, "E307", {"start": v(15.35, 10.1) * mm, "end": v(10.2, 4.95) * mm});
            skLineSegment(sketch, "E308", {"start": v(10.2, 4.95) * mm, "end": v(4.95, 4.95) * mm});
            skLineSegment(sketch, "E309", {"start": v(4.95, 4.95) * mm, "end": v(4.95, 10.2) * mm});
            skLineSegment(sketch, "E310", {"start": v(4.95, 10.2) * mm, "end": v(10.1, 15.35) * mm});
            skLineSegment(sketch, "E311", {"start": v(10.1, 15.35) * mm, "end": v(10.1, 10.1) * mm});
            skLineSegment(sketch, "E312", {"start": v(10.1, 10.1) * mm, "end": v(15.35, 10.1) * mm});
            skLineSegment(sketch, "E313", {"start": v(-4.95, 11.95) * mm, "end": v(-10.1, 17.1) * mm});
            skLineSegment(sketch, "E314", {"start": v(-10.1, 17.1) * mm, "end": v(-10.1, 24.39) * mm});
            skLineSegment(sketch, "E315", {"start": v(-10.1, 24.39) * mm, "end": v(-4.95, 19.23) * mm});
            skLineSegment(sketch, "E316", {"start": v(-4.95, 19.23) * mm, "end": v(-4.95, 11.95) * mm});
            skLineSegment(sketch, "E317", {"start": v(-4.95, 10.2) * mm, "end": v(-4.95, 4.95) * mm});
            skLineSegment(sketch, "E318", {"start": v(-4.95, 4.95) * mm, "end": v(-10.2, 4.95) * mm});
            skLineSegment(sketch, "E319", {"start": v(-10.2, 4.95) * mm, "end": v(-15.35, 10.1) * mm});
            skLineSegment(sketch, "E320", {"start": v(-15.35, 10.1) * mm, "end": v(-10.1, 10.1) * mm});
            skLineSegment(sketch, "E321", {"start": v(-10.1, 10.1) * mm, "end": v(-10.1, 15.35) * mm});
            skLineSegment(sketch, "E322", {"start": v(-10.1, 15.35) * mm, "end": v(-4.95, 10.2) * mm});
            skLineSegment(sketch, "E323", {"start": v(-17.1, 10.1) * mm, "end": v(-11.95, 4.95) * mm});
            skLineSegment(sketch, "E324", {"start": v(-11.95, 4.95) * mm, "end": v(-19.23, 4.95) * mm});
            skLineSegment(sketch, "E325", {"start": v(-19.23, 4.95) * mm, "end": v(-24.39, 10.1) * mm});
            skLineSegment(sketch, "E326", {"start": v(-24.39, 10.1) * mm, "end": v(-17.1, 10.1) * mm});
            skLineSegment(sketch, "E327", {"start": v(-19.23, -4.95) * mm, "end": v(-11.95, -4.95) * mm});
            skLineSegment(sketch, "E328", {"start": v(-11.95, -4.95) * mm, "end": v(-17.1, -10.1) * mm});
            skLineSegment(sketch, "E329", {"start": v(-17.1, -10.1) * mm, "end": v(-24.39, -10.1) * mm});
            skLineSegment(sketch, "E330", {"start": v(-24.39, -10.1) * mm, "end": v(-19.23, -4.95) * mm});
            skLineSegment(sketch, "E331", {"start": v(-16.67, -11.42) * mm, "end": v(-16.59, -11.34) * mm});
            skLineSegment(sketch, "E332", {"start": v(-16.59, -11.34) * mm, "end": v(-11.34, -11.34) * mm});
            skLineSegment(sketch, "E333", {"start": v(-11.34, -11.34) * mm, "end": v(-11.34, -16.59) * mm});
            skLineSegment(sketch, "E334", {"start": v(-11.34, -16.59) * mm, "end": v(-11.42, -16.67) * mm});
            skLineSegment(sketch, "E335", {"start": v(-11.42, -16.67) * mm, "end": v(-16.86, -16.86) * mm});
            skLineSegment(sketch, "E336", {"start": v(-16.86, -16.86) * mm, "end": v(-16.67, -11.42) * mm});
            skLineSegment(sketch, "E337", {"start": v(-15.35, -10.1) * mm, "end": v(-10.2, -4.95) * mm});
            skLineSegment(sketch, "E338", {"start": v(-10.2, -4.95) * mm, "end": v(-4.95, -4.95) * mm});
            skLineSegment(sketch, "E339", {"start": v(-4.95, -4.95) * mm, "end": v(-4.95, -10.2) * mm});
            skLineSegment(sketch, "E340", {"start": v(-4.95, -10.2) * mm, "end": v(-10.1, -15.35) * mm});
            skLineSegment(sketch, "E341", {"start": v(-10.1, -15.35) * mm, "end": v(-10.1, -10.1) * mm});
            skLineSegment(sketch, "E342", {"start": v(-10.1, -10.1) * mm, "end": v(-15.35, -10.1) * mm});
            skLineSegment(sketch, "E343", {"start": v(4.95, -11.95) * mm, "end": v(10.1, -17.1) * mm});
            skLineSegment(sketch, "E344", {"start": v(10.1, -17.1) * mm, "end": v(10.1, -24.38) * mm});
            skLineSegment(sketch, "E345", {"start": v(10.1, -24.38) * mm, "end": v(4.95, -19.23) * mm});
            skLineSegment(sketch, "E346", {"start": v(4.95, -19.23) * mm, "end": v(4.95, -11.95) * mm});
            skLineSegment(sketch, "E347", {"start": v(4.95, -10.2) * mm, "end": v(4.95, -4.95) * mm});
            skLineSegment(sketch, "E348", {"start": v(4.95, -4.95) * mm, "end": v(10.2, -4.95) * mm});
            skLineSegment(sketch, "E349", {"start": v(10.2, -4.95) * mm, "end": v(15.35, -10.1) * mm});
            skLineSegment(sketch, "E350", {"start": v(15.35, -10.1) * mm, "end": v(10.1, -10.1) * mm});
            skLineSegment(sketch, "E351", {"start": v(10.1, -10.1) * mm, "end": v(10.1, -15.35) * mm});
            skLineSegment(sketch, "E352", {"start": v(10.1, -15.35) * mm, "end": v(4.95, -10.2) * mm});
            skLineSegment(sketch, "E353", {"start": v(17.1, -10.1) * mm, "end": v(11.95, -4.95) * mm});
            skLineSegment(sketch, "E354", {"start": v(11.95, -4.95) * mm, "end": v(19.23, -4.95) * mm});
            skLineSegment(sketch, "E355", {"start": v(19.23, -4.95) * mm, "end": v(24.38, -10.1) * mm});
            skLineSegment(sketch, "E356", {"start": v(24.38, -10.1) * mm, "end": v(17.1, -10.1) * mm});
            skLineSegment(sketch, "E357", {"start": v(25.66, -9.63) * mm, "end": v(20.68, -4.64) * mm});
            skLineSegment(sketch, "E358", {"start": v(20.68, -4.64) * mm, "end": v(25.65, 0) * mm});
            skLineSegment(sketch, "E359", {"start": v(25.65, 0) * mm, "end": v(20.68, 4.64) * mm});
            skLineSegment(sketch, "E360", {"start": v(20.68, 4.64) * mm, "end": v(25.66, 9.63) * mm});
            skLineSegment(sketch, "E361", {"start": v(25.66, 9.63) * mm, "end": v(35.29, 0) * mm});
            skLineSegment(sketch, "E362", {"start": v(35.29, 0) * mm, "end": v(25.66, -9.63) * mm});
            skLineSegment(sketch, "E363", {"start": v(24.95, 11.34) * mm, "end": v(17.9, 11.34) * mm});
            skLineSegment(sketch, "E364", {"start": v(17.9, 11.34) * mm, "end": v(18.14, 18.14) * mm});
            skLineSegment(sketch, "E365", {"start": v(18.14, 18.14) * mm, "end": v(11.34, 17.9) * mm});
            skLineSegment(sketch, "E366", {"start": v(11.34, 17.9) * mm, "end": v(11.34, 24.95) * mm});
            skLineSegment(sketch, "E367", {"start": v(11.34, 24.95) * mm, "end": v(24.95, 24.95) * mm});
            skLineSegment(sketch, "E368", {"start": v(24.95, 24.95) * mm, "end": v(24.95, 11.34) * mm});
            skLineSegment(sketch, "E369", {"start": v(0, 35.29) * mm, "end": v(9.63, 25.66) * mm});
            skLineSegment(sketch, "E370", {"start": v(9.63, 25.66) * mm, "end": v(4.64, 20.68) * mm});
            skLineSegment(sketch, "E371", {"start": v(4.64, 20.68) * mm, "end": v(0, 25.65) * mm});
            skLineSegment(sketch, "E372", {"start": v(0, 25.65) * mm, "end": v(-4.64, 20.68) * mm});
            skLineSegment(sketch, "E373", {"start": v(-4.64, 20.68) * mm, "end": v(-9.63, 25.66) * mm});
            skLineSegment(sketch, "E374", {"start": v(-9.63, 25.66) * mm, "end": v(0, 35.29) * mm});
            skLineSegment(sketch, "E375", {"start": v(-24.95, 24.95) * mm, "end": v(-11.34, 24.95) * mm});
            skLineSegment(sketch, "E376", {"start": v(-11.34, 24.95) * mm, "end": v(-11.34, 17.9) * mm});
            skLineSegment(sketch, "E377", {"start": v(-11.34, 17.9) * mm, "end": v(-18.14, 18.14) * mm});
            skLineSegment(sketch, "E378", {"start": v(-18.14, 18.14) * mm, "end": v(-17.9, 11.34) * mm});
            skLineSegment(sketch, "E379", {"start": v(-17.9, 11.34) * mm, "end": v(-24.95, 11.34) * mm});
            skLineSegment(sketch, "E380", {"start": v(-24.95, 11.34) * mm, "end": v(-24.95, 24.95) * mm});
            skLineSegment(sketch, "E381", {"start": v(-25.66, 9.63) * mm, "end": v(-20.68, 4.64) * mm});
            skLineSegment(sketch, "E382", {"start": v(-20.68, 4.64) * mm, "end": v(-25.65, 0) * mm});
            skLineSegment(sketch, "E383", {"start": v(-25.65, 0) * mm, "end": v(-20.68, -4.64) * mm});
            skLineSegment(sketch, "E384", {"start": v(-20.68, -4.64) * mm, "end": v(-25.66, -9.63) * mm});
            skLineSegment(sketch, "E385", {"start": v(-25.66, -9.63) * mm, "end": v(-35.29, 0) * mm});
            skLineSegment(sketch, "E386", {"start": v(-35.29, 0) * mm, "end": v(-25.66, 9.63) * mm});
            skLineSegment(sketch, "E387", {"start": v(0, -35.29) * mm, "end": v(-9.63, -25.66) * mm});
            skLineSegment(sketch, "E388", {"start": v(-9.63, -25.66) * mm, "end": v(-4.64, -20.68) * mm});
            skLineSegment(sketch, "E389", {"start": v(-4.64, -20.68) * mm, "end": v(0, -25.65) * mm});
            skLineSegment(sketch, "E390", {"start": v(0, -25.65) * mm, "end": v(4.64, -20.68) * mm});
            skLineSegment(sketch, "E391", {"start": v(4.64, -20.68) * mm, "end": v(9.63, -25.66) * mm});
            skLineSegment(sketch, "E392", {"start": v(9.63, -25.66) * mm, "end": v(0, -35.29) * mm});
            skLineSegment(sketch, "E393", {"start": v(24.95, -24.95) * mm, "end": v(11.34, -24.95) * mm});
            skLineSegment(sketch, "E394", {"start": v(11.34, -24.95) * mm, "end": v(11.34, -17.9) * mm});
            skLineSegment(sketch, "E395", {"start": v(11.34, -17.9) * mm, "end": v(18.14, -18.14) * mm});
            skLineSegment(sketch, "E396", {"start": v(18.14, -18.14) * mm, "end": v(17.9, -11.34) * mm});
            skLineSegment(sketch, "E397", {"start": v(17.9, -11.34) * mm, "end": v(24.95, -11.34) * mm});
            skLineSegment(sketch, "E398", {"start": v(24.95, -11.34) * mm, "end": v(24.95, -24.95) * mm});
            skLineSegment(sketch, "E399.MirrorCS", {"start": v(-11.34, -24.95) * mm, "end": v(-24.95, -24.95) * mm});
            skLineSegment(sketch, "E400.MirrorCS", {"start": v(-11.34, -17.9) * mm, "end": v(-11.34, -24.95) * mm});
            skLineSegment(sketch, "E401.MirrorCS", {"start": v(-11.34, -17.9) * mm, "end": v(-18.14, -18.14) * mm});
            skLineSegment(sketch, "E402.MirrorCS", {"start": v(-18.14, -18.14) * mm, "end": v(-17.9, -11.34) * mm});
            skLineSegment(sketch, "E403.MirrorCS", {"start": v(-24.95, -24.95) * mm, "end": v(-24.95, -11.34) * mm});
            skLineSegment(sketch, "E404.MirrorCS", {"start": v(-17.9, -11.34) * mm, "end": v(-24.95, -11.34) * mm});
            skLineSegment(sketch, "E405.MirrorCS", {"start": v(-16.85, 16.86) * mm, "end": v(-11.42, 16.67) * mm});
            skLineSegment(sketch, "E406.MirrorCS", {"start": v(-11.34, 16.59) * mm, "end": v(-11.34, 11.34) * mm});
            skLineSegment(sketch, "E407.MirrorCS", {"start": v(-11.34, 11.34) * mm, "end": v(-16.59, 11.34) * mm});
            skLineSegment(sketch, "E408.MirrorCS", {"start": v(-16.67, 11.42) * mm, "end": v(-16.85, 16.86) * mm});
            skLineSegment(sketch, "E409", {"start": v(-11.42, 16.67) * mm, "end": v(-11.34, 16.59) * mm});
            skLineSegment(sketch, "E410", {"start": v(-16.67, 11.42) * mm, "end": v(-16.59, 11.34) * mm});
            skCircle(sketch, "E411", {"center": v(0, 0) * mm, "radius": 44.45 * mm});
            skSolve(sketch);
        }
        {
            var Q0;
            Q0=qSketchRegion(id+"F2",true);
            extrude(context, id + "F3", {"entities" : qUnion([Q0]), "operationType" : NewBodyOperationType.INTERSECT, "endBound" : BoundingType.UP_TO_NEXT, "oppositeDirection" : true, "depth" : 25.4 * mm});
        }
    });
